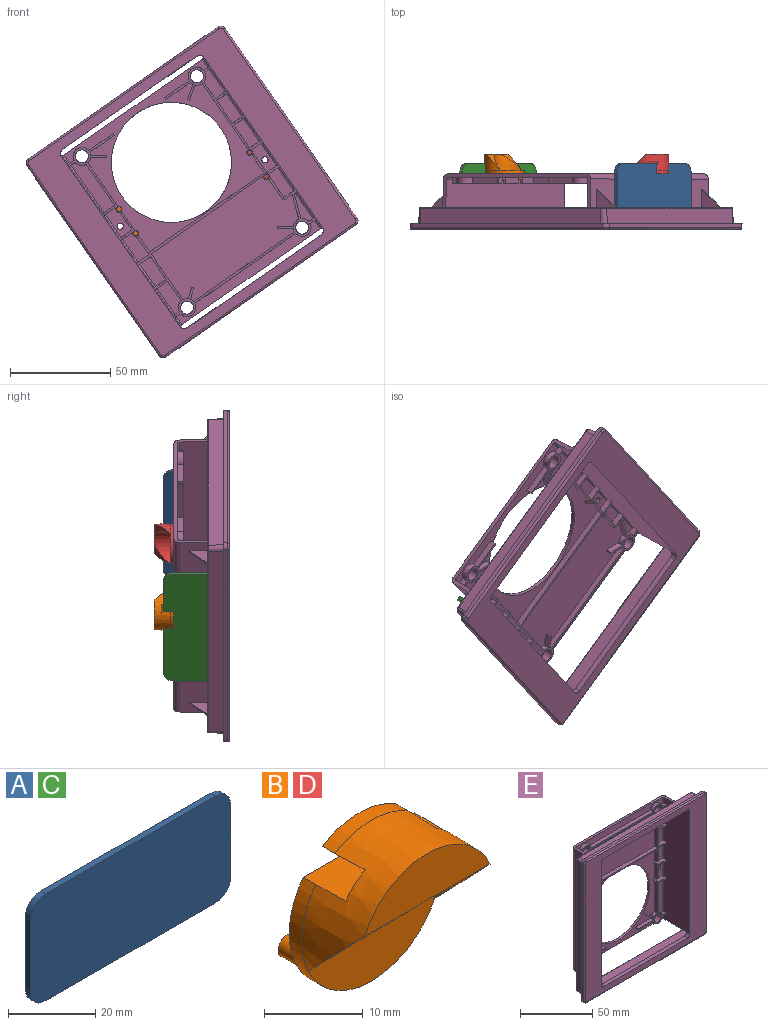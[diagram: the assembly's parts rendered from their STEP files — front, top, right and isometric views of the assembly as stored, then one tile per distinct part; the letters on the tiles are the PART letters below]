
ASSEMBLY  parts=5 mates=6
PART A: 10 faces, bbox 65x1.6x30 mm
  f0: plane 20x1.6mm, normal (1,0,0), area 32mm2, adj f1,f7,f8,f9
  f1: cylinder r=5mm len=5mm, axis (0,1,0), area 12.6mm2, adj f0,f2,f8,f9
  f2: plane 55x1.6mm, normal (0,0,1), area 88mm2, adj f1,f3,f8,f9
  f3: cylinder r=5mm len=5mm, axis (0,1,0), area 12.6mm2, adj f2,f4,f8,f9
  f4: plane 20x1.6mm, normal (-1,0,0), area 32mm2, adj f3,f5,f8,f9
  f5: cylinder r=5mm len=5mm, axis (0,1,0), area 12.6mm2, adj f4,f6,f8,f9
  f6: plane 55x1.6mm, normal (0,0,-1), area 88mm2, adj f5,f7,f8,f9
  f7: cylinder r=5mm len=5mm, axis (0,1,0), area 12.6mm2, adj f0,f6,f8,f9
  f8: plane 65x30mm, normal (0,-1,0), area 1928.5mm2, adj f0,f1,f2,f3,f4,f5,f6,f7
  f9: plane 65x30mm, normal (0,1,0), area 1928.5mm2, adj f0,f1,f2,f3,f4,f5,f6,f7
PART B: 18 faces, bbox 20x12.8x20 mm
  f0: plane 20x16mm, normal (0,1,0), area 252.1mm2, adj f4,f6,f7,f9,f14
  f1: plane 10.54x1.5mm, normal (0,1,0), area 10.7mm2, adj f5,f13
  f2: cone r=10mm half-angle=1deg, axis (0,1,0), area 219.9mm2, adj f4,f5,f12,f13,f14,f15,f16,f17
  f3: plane 18.1x14mm, normal (0,-1,0), area 181.7mm2, adj f4,f6,f11
  f4: cylinder r=10mm len=20mm, axis (0,-1,0), area 79.7mm2, adj f0,f2,f3,f14
  f5: cylinder r=10mm len=10.54mm, axis (0,-1,0), area 20mm2, adj f1,f2,f13
  f6: cylinder r=1.55mm len=3.1mm, axis (0,-1,0), area 17.5mm2, adj f0,f3
  f7: cylinder r=1.25mm len=3mm, axis (0,-1,0), area 23.6mm2, adj f0,f8
  f8: plane 2.5x2.5mm, normal (0,1,0), area 4.9mm2, adj f7
  f9: cylinder r=1.25mm len=3mm, axis (0,-1,0), area 23.6mm2, adj f0,f10
  f10: plane 2.5x2.5mm, normal (0,1,0), area 4.9mm2, adj f9
  f11: cone r=9.09mm half-angle=1deg, axis (0,-1,0), area 139.7mm2, adj f3,f12,f16,f17
  f12: plane 17.99x5.83mm, normal (0,-1,0), area 75.2mm2, adj f2,f11,f16,f17
  f13: plane 10.54x6mm, normal (0,0,-1), area 62.6mm2, adj f1,f2,f5,f15
  f14: plane 16x6mm, normal (0,0,1), area 95.6mm2, adj f0,f2,f4,f15
  f15: plane 15.82x2.5mm, normal (0,1,0), area 33.5mm2, adj f2,f13,f14
  f16: plane 8.54x8.28mm, normal (0,-0.72,-0.69), area 29.8mm2, adj f2,f11,f12
  f17: plane 8.54x8.28mm, normal (0,-0.72,-0.69), area 29.8mm2, adj f2,f11,f12
PART C: same geometry as A
PART D: same geometry as B
PART E: 266 faces, bbox 121.1x27.9x121.1 mm
  f0: plane 85.9x49.43mm, normal (0,-1,0), area 331.9mm2, adj f4,f6,f27,f37,f50,f51,f53,f54
  f1: plane 12x8.52mm, normal (0,-1,0), area 20.6mm2, adj f5,f7,f27,f155,f156,f166,f218,f219
  f2: plane 35.28x27.37mm, normal (0,-1,0), area 91.9mm2, adj f26,f27,f56,f60,f108,f115,f117,f118
  f3: plane 40.31x3mm, normal (1,-0.01,0), area 120.9mm2, adj f25,f49,f113,f216
  f4: plane 10.24x3mm, normal (-1,-0.01,0), area 30.7mm2, adj f0,f49,f162,f219
  f5: plane 11.86x3mm, normal (-1,-0.01,0), area 35.6mm2, adj f1,f49,f218,f219
  f6: plane 11.17x3.01mm, normal (1,-0.01,0), area 33.5mm2, adj f0,f47,f160,f219
  f7: plane 10.89x3.01mm, normal (1,-0.01,0), area 32.6mm2, adj f1,f48,f156,f218
  f8: plane 9.15x2.5mm, normal (0,1,0), area 22.9mm2, adj f18,f190,f212,f213
  f9: plane 90.76x6.11mm, normal (0,1,0), area 553.7mm2, adj f11,f19,f190,f214,f252,f254
  f10: plane 8x2.5mm, normal (0,1,0), area 20mm2, adj f11,f18,f205,f206
  f11: plane 17.24x10.76mm, normal (0,0.01,-1), area 119.9mm2, adj f9,f10,f18,f193,f205,f214,f215,f254
  f12: plane 90.76x6.11mm, normal (0,1,0), area 553.7mm2, adj f15,f21,f187,f203,f258,f264
  f13: plane 10x2.5mm, normal (0,1,0), area 25mm2, adj f22,f187,f201,f202
  f14: plane 70x2.5mm, normal (0,1,0), area 175mm2, adj f22,f197,f198,f199
  f15: plane 17.24x10.76mm, normal (0,0.01,1), area 119.9mm2, adj f12,f22,f23,f185,f194,f203,f204,f264
  f16: plane 7.72x7.51mm, normal (1,0.02,0), area 57.6mm2, adj f17,f91,f247,f256
  f17: plane 111.01x8.88mm, normal (0,1,0), area 303.6mm2, adj f16,f18,f22,f78,f79,f80,f90,f91
  f18: plane 104x22.15mm, normal (-1,0.02,0), area 2260mm2, adj f8,f10,f11,f17,f20,f65,f102,f105
  f19: plane 89.95x7.51mm, normal (1,0.02,0), area 674.8mm2, adj f9,f248,f252,f254
  f20: plane 70x2.5mm, normal (0,1,0), area 175mm2, adj f18,f208,f209,f210
  f21: plane 89.95x7.51mm, normal (-1,0.02,0), area 674.8mm2, adj f12,f249,f258,f264
  f22: plane 104x22.15mm, normal (1,0.02,0), area 2260mm2, adj f13,f14,f15,f17,f23,f65,f100,f105
  f23: plane 7.15x2.5mm, normal (0,1,0), area 17.9mm2, adj f15,f22,f194,f195
  f24: plane 7.72x7.51mm, normal (-1,0.02,0), area 57.6mm2, adj f65,f95,f239,f262
  f25: cone r=4.45mm half-angle=0.5deg, axis (0,1,0), area 11.4mm2, adj f3,f49,f113,f137
  f26: cone r=4.45mm half-angle=0.5deg, axis (0,1,0), area 9.4mm2, adj f2,f49,f135,f165
  f27: plane 104.01x25.12mm, normal (-1,-0.02,0), area 2589.2mm2, adj f0,f1,f2,f28,f29,f30,f31,f59
  f28: cylinder r=0.9mm len=13.9mm, axis (0,0,-1), area 19.4mm2, adj f27,f48,f153,f156
  f29: cylinder r=0.9mm len=13.9mm, axis (0,0,-1), area 19.4mm2, adj f27,f47,f155,f160
  f30: cylinder r=0.9mm len=15.91mm, axis (0,0,-1), area 22.2mm2, adj f27,f45,f129,f157
  f31: cylinder r=0.9mm len=13.9mm, axis (0,0,-1), area 19.4mm2, adj f27,f46,f158,f159
  f32: cylinder r=0.9mm len=13.9mm, axis (0,0,-1), area 19.4mm2, adj f41,f81,f170,f180
  f33: cylinder r=0.9mm len=13.9mm, axis (0,0,-1), area 19.4mm2, adj f42,f81,f171,f172
  f34: cylinder r=0.9mm len=13.9mm, axis (0,0,-1), area 19.4mm2, adj f39,f81,f179,f182
  f35: cylinder r=0.9mm len=13.9mm, axis (0,0,-1), area 19.4mm2, adj f40,f81,f178,f181
  f36: cylinder r=0.9mm len=13.91mm, axis (0,0,-1), area 19.4mm2, adj f38,f81,f133,f183
  f37: cone r=4.45mm half-angle=0.5deg, axis (0,1,0), area 14.2mm2, adj f0,f43,f124,f173
  f38: plane 13.9x5.86mm, normal (0,-1,0), area 72.7mm2, adj f36,f55,f133,f150,f183
  f39: plane 13.9x5.86mm, normal (0,-1,0), area 81.4mm2, adj f34,f145,f179,f182
  f40: plane 13.9x5.86mm, normal (0,-1,0), area 81.4mm2, adj f35,f147,f178,f181
  f41: plane 13.9x5.86mm, normal (0,-1,0), area 73.7mm2, adj f32,f146,f170,f180,f216,f220
  f42: plane 13.9x5.86mm, normal (0,-1,0), area 81.2mm2, adj f33,f148,f171,f172,f217
  f43: plane 74.8x31.75mm, normal (0,-1,0), area 2199.7mm2, adj f37,f50,f51,f112,f123,f124,f125,f141
  f44: plane 15.9x4.98mm, normal (0,-1,0), area 45.3mm2, adj f62,f63,f126,f174,f175
  f45: plane 15.9x6.51mm, normal (0,-1,0), area 92.4mm2, adj f30,f114,f129,f157,f164
  f46: plane 13.9x6.51mm, normal (0,-1,0), area 90.5mm2, adj f31,f158,f159,f167
  f47: plane 13.9x6.51mm, normal (0,-1,0), area 88.9mm2, adj f6,f29,f155,f160,f166,f219
  f48: plane 13.9x6.51mm, normal (0,-1,0), area 81.3mm2, adj f7,f28,f153,f156,f168,f218,f221
  f49: plane 84.02x64.2mm, normal (0,-1,0), area 1560.5mm2, adj f3,f4,f5,f25,f26,f57,f58,f60
  f50: cylinder r=4.45mm len=3mm, axis (0,1,0), area 8.3mm2, adj f0,f43,f142,f163
  f51: cylinder r=4.45mm len=3mm, axis (0,1,0), area 6mm2, adj f0,f43,f141,f143
  f52: plane 84.02x5.05mm, normal (0,-1,0), area 371.7mm2, adj f53,f54,f61,f103,f105,f127,f128,f140
  f53: cone r=4.45mm half-angle=0.5deg, axis (0,1,0), area 38.6mm2, adj f0,f52,f127,f140
  f54: cone r=4.45mm half-angle=0.5deg, axis (0,1,0), area 38.6mm2, adj f0,f52,f128,f140
  f55: cone r=4.45mm half-angle=0.5deg, axis (0,1,0), area 15.8mm2, adj f38,f113,f133,f150
  f56: cone r=4.45mm half-angle=0.5deg, axis (0,1,0), area 17.8mm2, adj f2,f64,f130,f169
  f57: cylinder r=0.9mm len=5.07mm, axis (0,0,-1), area 7.1mm2, adj f49,f81,f106,f132
  f58: cone r=4.45mm half-angle=0.5deg, axis (0,1,0), area 38.8mm2, adj f49,f113,f121,f132
  f59: cylinder r=0.9mm len=28.91mm, axis (0,0,-1), area 40.4mm2, adj f27,f64,f130,f154
  f60: cone r=4.45mm half-angle=0.5deg, axis (0,1,0), area 4.6mm2, adj f2,f49,f118,f134
  f61: cylinder r=0.9mm len=5.07mm, axis (0,0,-1), area 7.1mm2, adj f27,f52,f105,f128
  f62: cylinder r=0.9mm len=15.91mm, axis (0,0,-1), area 22.2mm2, adj f44,f81,f126,f175
  f63: cone r=4.45mm half-angle=0.5deg, axis (0,1,0), area 13mm2, adj f0,f44,f126,f174
  f64: plane 28.9x6.51mm, normal (0,-1,0), area 177mm2, adj f56,f59,f130,f154,f169
  f65: plane 111.01x8.88mm, normal (0,1,0), area 303.6mm2, adj f18,f22,f24,f76,f77,f82,f92,f93
  f66: plane 120.5x120.5mm, normal (0,1,0), area 1523.2mm2, adj f68,f69,f70,f71,f72,f73,f74,f75
  f67: plane 118.5x118.5mm, normal (0,-1,0), area 4621.4mm2, adj f27,f76,f77,f78,f79,f80,f81,f82
  f68: plane 115.5x2mm, normal (0,0,-1), area 231mm2, adj f66,f69,f75,f222
  f69: cylinder r=2.5mm len=2.5mm, axis (0,-1,0), area 7.9mm2, adj f66,f68,f70,f223
  f70: plane 115.5x2mm, normal (1,0,0), area 231mm2, adj f66,f69,f71,f225
  f71: cylinder r=2.5mm len=2.5mm, axis (0,-1,0), area 7.9mm2, adj f66,f70,f72,f227
  f72: plane 115.5x2mm, normal (0,0,1), area 231mm2, adj f66,f71,f73,f229
  f73: cylinder r=2.5mm len=2.5mm, axis (0,-1,0), area 7.9mm2, adj f66,f72,f74,f228
  f74: plane 115.5x2mm, normal (-1,0,0), area 231mm2, adj f66,f73,f75,f226
  f75: cylinder r=2.5mm len=2.5mm, axis (0,-1,0), area 7.9mm2, adj f66,f68,f74,f224
  f76: plane 81.7x3mm, normal (0,-0.02,1), area 245.1mm2, adj f65,f67,f77,f82
  f77: cone r=2.5mm half-angle=1deg, axis (0,-1,0), area 11.7mm2, adj f27,f65,f67,f76
  f78: cone r=2.5mm half-angle=1deg, axis (0,-1,0), area 11.7mm2, adj f17,f27,f67,f79
  f79: plane 81.7x3mm, normal (0,-0.02,-1), area 245.1mm2, adj f17,f67,f78,f80
  f80: cone r=2.5mm half-angle=1deg, axis (0,-1,0), area 11.7mm2, adj f17,f67,f79,f81
  f81: plane 104.01x25.12mm, normal (1,-0.02,0), area 2586.7mm2, adj f0,f32,f33,f34,f35,f36,f57,f62
  f82: cone r=2.5mm half-angle=1deg, axis (0,-1,0), area 11.7mm2, adj f65,f67,f76,f81
  f83: plane 109.5x7.51mm, normal (0,0.02,-1), area 822.3mm2, adj f66,f84,f98,f237
  f84: cone r=2.25mm half-angle=1deg, axis (0,-1,0), area 25.8mm2, adj f66,f83,f85,f235
  f85: plane 109.5x7.51mm, normal (-1,0.02,0), area 822.3mm2, adj f66,f84,f86,f233
  f86: cone r=2.25mm half-angle=1deg, axis (0,-1,0), area 25.8mm2, adj f66,f85,f87,f231
  f87: plane 109.5x7.51mm, normal (0,0.02,1), area 822.3mm2, adj f66,f86,f88,f230
  f88: cone r=2.25mm half-angle=1deg, axis (0,-1,0), area 25.8mm2, adj f66,f87,f89,f232
  f89: plane 109.5x7.51mm, normal (1,0.02,0), area 822.3mm2, adj f66,f88,f98,f234
  f90: plane 109.5x7.51mm, normal (0,0.02,-1), area 822.3mm2, adj f17,f91,f97,f245
  f91: cone r=0.75mm half-angle=1deg, axis (0,1,0), area 9.6mm2, adj f16,f17,f90,f246
  f92: plane 7.72x7.51mm, normal (1,0.02,0), area 57.6mm2, adj f65,f93,f238,f250
  f93: cone r=0.75mm half-angle=1deg, axis (0,1,0), area 9.6mm2, adj f65,f92,f94,f240
  f94: plane 109.5x7.51mm, normal (0,0.02,1), area 822.3mm2, adj f65,f93,f95,f242
  f95: cone r=0.75mm half-angle=1deg, axis (0,1,0), area 9.6mm2, adj f24,f65,f94,f241
  f96: plane 7.72x7.51mm, normal (-1,0.02,0), area 57.6mm2, adj f17,f97,f243,f260
  f97: cone r=0.75mm half-angle=1deg, axis (0,1,0), area 9.6mm2, adj f17,f90,f96,f244
  f98: cone r=2.25mm half-angle=1deg, axis (0,-1,0), area 25.8mm2, adj f66,f83,f89,f236
  f99: plane 112.79x112.79mm, normal (0,1,0), area 109.6mm2, adj f185,f188,f191,f193,f230,f231,f232,f233
  f100: cylinder r=2.7mm len=103.23mm, axis (0,0,-1), area 432.7mm2, adj f22,f101,f105,f106
  f101: plane 103.13x84.02mm, normal (0,1,0), area 5662.2mm2, adj f100,f102,f105,f106,f107,f108,f109,f110
  f102: cylinder r=2.7mm len=103.23mm, axis (0,0,-1), area 432.7mm2, adj f18,f101,f105,f106
  f103: cylinder r=0.9mm len=5.07mm, axis (0,0,-1), area 7.1mm2, adj f52,f81,f105,f127
  f104: cylinder r=0.9mm len=5.07mm, axis (0,0,-1), area 7.1mm2, adj f27,f49,f106,f131
  f105: plane 90.22x24.82mm, normal (0,0.02,1), area 241.1mm2, adj f17,f18,f22,f27,f52,f61,f81,f100
  f106: plane 90.22x24.82mm, normal (0,0.02,-1), area 241mm2, adj f18,f22,f27,f49,f57,f65,f81,f100
  f107: cylinder r=3.25mm len=6.5mm, axis (0,-1,0), area 98mm2, adj f0,f101
  f108: cylinder r=3.25mm len=6.5mm, axis (0,-1,0), area 98mm2, adj f2,f101
  f109: cylinder r=30mm len=60mm, axis (0,-1,0), area 339.3mm2, adj f49,f101
  f110: cylinder r=3.25mm len=6.5mm, axis (0,-1,0), area 98mm2, adj f101,f113
  f111: cylinder r=3.25mm len=6.5mm, axis (0,-1,0), area 98mm2, adj f0,f101
  f112: cone r=4.45mm half-angle=0.5deg, axis (0,1,0), area 4.9mm2, adj f0,f43,f123,f141
  f113: plane 49.97x27.37mm, normal (0,-1,0), area 121.2mm2, adj f3,f25,f55,f58,f81,f110,f116,f120
  f114: cone r=4.45mm half-angle=0.5deg, axis (0,1,0), area 17.8mm2, adj f0,f45,f129,f164
  f115: cone r=4.45mm half-angle=0.5deg, axis (0,1,0), area 38.9mm2, adj f2,f49,f117,f131
  f116: cone r=4.45mm half-angle=0.5deg, axis (0,1,0), area 4.7mm2, adj f49,f113,f120,f138
  f117: plane 15.05x3mm, normal (0,-0.01,-1), area 45.1mm2, adj f2,f49,f115,f119
  f118: plane 15.07x3mm, normal (0,-0.01,1), area 45.1mm2, adj f2,f49,f60,f119
  f119: plane 3x1.1mm, normal (-1,-0.01,0), area 3.2mm2, adj f2,f49,f117,f118
  f120: plane 15.07x3mm, normal (0,-0.01,1), area 45.1mm2, adj f49,f113,f116,f122
  f121: plane 15.05x3mm, normal (0,-0.01,-1), area 45.1mm2, adj f49,f58,f113,f122
  f122: plane 3x1.1mm, normal (1,-0.01,0), area 3.2mm2, adj f49,f113,f120,f121
  f123: plane 6.62x4.61mm, normal (0.57,-0.01,0.82), area 24.1mm2, adj f0,f43,f112,f125
  f124: plane 6.59x4.64mm, normal (-0.57,-0.01,-0.82), area 24.1mm2, adj f0,f37,f43,f125
  f125: plane 3x0.9mm, normal (0.82,-0.01,-0.57), area 3.2mm2, adj f0,f43,f123,f124
  f126: plane 3.56x3mm, normal (0,-0.01,-1), area 10.4mm2, adj f0,f44,f62,f63,f81
  f127: plane 3.56x3mm, normal (0,-0.01,1), area 10.4mm2, adj f0,f52,f53,f81,f103
  f128: plane 3.56x3mm, normal (0,-0.01,1), area 10.4mm2, adj f0,f27,f52,f54,f61
  f129: plane 3.56x3mm, normal (0,-0.01,-1), area 10.4mm2, adj f0,f27,f30,f45,f114
  f130: plane 3.56x3mm, normal (0,-0.01,1), area 10.4mm2, adj f2,f27,f56,f59,f64
  f131: plane 3.56x3mm, normal (0,-0.01,-1), area 10.4mm2, adj f2,f27,f49,f104,f115
  f132: plane 3.56x3mm, normal (0,-0.01,-1), area 10.4mm2, adj f49,f57,f58,f81,f113
  f133: plane 3.56x3mm, normal (0,-0.01,1), area 10.4mm2, adj f36,f38,f55,f81,f113
  f134: plane 6.62x4.61mm, normal (-0.57,-0.01,-0.82), area 24.1mm2, adj f2,f49,f60,f136
  f135: plane 6.59x4.64mm, normal (0.57,-0.01,0.82), area 24.1mm2, adj f2,f26,f49,f136
  f136: plane 3x0.9mm, normal (-0.82,-0.01,0.57), area 3.2mm2, adj f2,f49,f134,f135
  f137: plane 6.59x4.64mm, normal (-0.57,-0.01,0.82), area 24.1mm2, adj f25,f49,f113,f139
  f138: plane 6.62x4.61mm, normal (0.57,-0.01,-0.82), area 24.1mm2, adj f49,f113,f116,f139
  f139: plane 3x0.9mm, normal (0.82,-0.01,0.57), area 3.2mm2, adj f49,f113,f137,f138
  f140: plane 61.21x3mm, normal (0,-0.01,1), area 183.6mm2, adj f0,f52,f53,f54
  f141: plane 61.19x3mm, normal (0,-0.01,-1), area 183.5mm2, adj f0,f43,f51,f112
  f142: plane 4.64x3.88mm, normal (0.64,-0.01,-0.77), area 18.1mm2, adj f0,f43,f50,f144
  f143: plane 4.65x3.86mm, normal (-0.64,-0.01,0.77), area 18.1mm2, adj f0,f43,f51,f144
  f144: plane 3x0.85mm, normal (-0.77,-0.01,-0.64), area 3.2mm2, adj f0,f43,f142,f143
  f145: plane 13.9x3mm, normal (-1,-0.01,0), area 41.7mm2, adj f39,f113,f179,f182
  f146: plane 12.55x3.04mm, normal (-1,-0.01,0), area 37.4mm2, adj f0,f41,f170,f216
  f147: plane 13.9x3mm, normal (-1,-0.01,0), area 41.7mm2, adj f40,f113,f178,f181
  f148: plane 12.82x3.04mm, normal (-1,-0.01,0), area 38.3mm2, adj f0,f42,f172,f217
  f149: plane 10.91x3mm, normal (1,-0.01,0), area 32.7mm2, adj f0,f49,f162,f216
  f150: plane 10.17x3mm, normal (-1,-0.01,0), area 30.5mm2, adj f38,f55,f113,f183
  f151: plane 12.58x3mm, normal (1,-0.01,0), area 37.7mm2, adj f0,f43,f152,f217
  f152: plane 3x0.55mm, normal (0,0,1), area 1.6mm2, adj f0,f43,f151,f177
  f153: plane 7.47x3mm, normal (0,0,1), area 22.1mm2, adj f2,f27,f28,f48,f168
  f154: plane 7.47x3mm, normal (0,0,-1), area 22.1mm2, adj f2,f27,f59,f64,f169
  f155: plane 7.47x3mm, normal (0,0,1), area 22.1mm2, adj f1,f27,f29,f47,f166
  f156: plane 7.47x3mm, normal (0,0,-1), area 22.1mm2, adj f1,f7,f27,f28,f48
  f157: plane 7.47x3mm, normal (0,0,1), area 22.1mm2, adj f0,f27,f30,f45,f164
  f158: plane 7.47x3mm, normal (0,0,-1), area 22.1mm2, adj f0,f27,f31,f46,f167
  f159: plane 7.47x3mm, normal (0,0,1), area 22.1mm2, adj f0,f27,f31,f46,f167
  f160: plane 7.47x3mm, normal (0,0,-1), area 22.1mm2, adj f0,f6,f27,f29,f47
  f161: plane 68.42x3mm, normal (0,0,1), area 205.2mm2, adj f0,f43,f163,f217
  f162: plane 69.51x3mm, normal (0,0,-1), area 208.4mm2, adj f0,f4,f49,f149
  f163: plane 27.89x3mm, normal (-1,-0.01,0), area 83.7mm2, adj f0,f43,f50,f161
  f164: plane 12.05x3mm, normal (1,-0.01,0), area 36.1mm2, adj f0,f45,f114,f157
  f165: plane 26.4x3mm, normal (-1,-0.01,0), area 79.1mm2, adj f2,f26,f49,f218
  f166: plane 3.01x0.04mm, normal (1,-0.01,0), area 0.1mm2, adj f1,f47,f155,f219
  f167: plane 13.9x3mm, normal (1,-0.01,0), area 41.7mm2, adj f0,f46,f158,f159
  f168: plane 3.01x0.32mm, normal (1,-0.01,0), area 0.9mm2, adj f2,f48,f153,f218
  f169: plane 25.05x3mm, normal (1,-0.01,0), area 75.1mm2, adj f2,f56,f64,f154
  f170: plane 6.82x3mm, normal (0,0,-1), area 20.2mm2, adj f0,f32,f41,f81,f146
  f171: plane 6.65x3mm, normal (0,0,1), area 19.7mm2, adj f0,f33,f42,f81,f217
  f172: plane 6.82x3mm, normal (0,0,-1), area 20.2mm2, adj f0,f33,f42,f81,f148
  f173: plane 12.14x4.44mm, normal (0.94,-0.01,-0.34), area 38.7mm2, adj f0,f37,f43,f176
  f174: plane 12.5x4.58mm, normal (-0.94,-0.01,0.34), area 39.9mm2, adj f0,f44,f63,f175
  f175: plane 3x1.4mm, normal (0,0,1), area 3.9mm2, adj f0,f44,f62,f81,f174
  f176: plane 4.82x3mm, normal (0,0,1), area 14.4mm2, adj f0,f43,f173,f177
  f177: plane 3x0.55mm, normal (1,0,0), area 1.6mm2, adj f0,f43,f152,f176
  f178: plane 6.82x3mm, normal (0,0,1), area 20.2mm2, adj f35,f40,f81,f113,f147
  f179: plane 6.82x3mm, normal (0,0,-1), area 20.2mm2, adj f34,f39,f81,f113,f145
  f180: plane 6.76x3mm, normal (0,0,1), area 20mm2, adj f32,f41,f81,f113,f216
  f181: plane 6.82x3mm, normal (0,0,-1), area 20.2mm2, adj f35,f40,f81,f113,f147
  f182: plane 6.82x3mm, normal (0,0,1), area 20.2mm2, adj f34,f39,f81,f113,f145
  f183: plane 6.82x3mm, normal (0,0,-1), area 20.2mm2, adj f36,f38,f81,f113,f150
  f184: plane 17.24x10.76mm, normal (0,0.01,-1), area 128.9mm2, adj f22,f65,f185,f262,f263
  f185: plane 10.85x9.11mm, normal (0.64,0.77,0), area 13.1mm2, adj f15,f22,f99,f184,f263,f265
  f186: plane 17.24x10.76mm, normal (0,0.01,1), area 128.9mm2, adj f17,f22,f188,f260,f261
  f187: plane 17.24x10.76mm, normal (0,0.01,-1), area 119.9mm2, adj f12,f13,f22,f188,f202,f203,f204,f258
  f188: plane 10.85x9.11mm, normal (0.64,0.77,0), area 13.1mm2, adj f22,f99,f186,f187,f259,f261
  f189: plane 17.24x10.76mm, normal (0,0.01,-1), area 128.9mm2, adj f18,f65,f191,f250,f251
  f190: plane 17.24x10.76mm, normal (0,0.01,1), area 119.9mm2, adj f8,f9,f18,f191,f213,f214,f215,f252
  f191: plane 10.85x9.11mm, normal (-0.64,0.77,0), area 13.1mm2, adj f18,f99,f189,f190,f251,f253
  f192: plane 17.24x10.76mm, normal (0,0.01,1), area 128.9mm2, adj f17,f18,f193,f256,f257
  f193: plane 10.85x9.11mm, normal (-0.64,0.77,0), area 13.1mm2, adj f11,f18,f99,f192,f255,f257
  f194: plane 7.22x5mm, normal (-1,0,0), area 35.9mm2, adj f15,f23,f195,f204
  f195: plane 5x2.5mm, normal (0,0,-1), area 12.5mm2, adj f23,f194,f196,f204
  f196: plane 5x1.8mm, normal (-1,0,0), area 9mm2, adj f22,f195,f197,f204
  f197: plane 5x2.5mm, normal (0,0,1), area 12.5mm2, adj f14,f196,f198,f204
  f198: plane 70x5mm, normal (-1,0,0), area 350mm2, adj f14,f197,f199,f204
  f199: plane 5x2.5mm, normal (0,0,-1), area 12.5mm2, adj f14,f198,f200,f204
  f200: plane 5x1.8mm, normal (-1,0,0), area 9mm2, adj f22,f199,f201,f204
  f201: plane 5x2.5mm, normal (0,0,1), area 12.5mm2, adj f13,f200,f202,f204
  f202: plane 10.07x5mm, normal (-1,0,0), area 50.2mm2, adj f13,f187,f201,f204
  f203: plane 90.88x5mm, normal (1,0,0), area 454.1mm2, adj f12,f15,f187,f204
  f204: plane 90.88x4.3mm, normal (0,1,0), area 172.6mm2, adj f15,f187,f194,f195,f196,f197,f198,f199
  f205: plane 8.07x5mm, normal (1,0,0), area 40.2mm2, adj f10,f11,f206,f215
  f206: plane 5x2.5mm, normal (0,0,1), area 12.5mm2, adj f10,f205,f207,f215
  f207: plane 5x1.8mm, normal (1,0,0), area 9mm2, adj f18,f206,f208,f215
  f208: plane 5x2.5mm, normal (0,0,-1), area 12.5mm2, adj f20,f207,f209,f215
  f209: plane 70x5mm, normal (1,0,0), area 350mm2, adj f20,f208,f210,f215
  f210: plane 5x2.5mm, normal (0,0,1), area 12.5mm2, adj f20,f209,f211,f215
  f211: plane 5x1.8mm, normal (1,0,0), area 9mm2, adj f18,f210,f212,f215
  f212: plane 5x2.5mm, normal (0,0,-1), area 12.5mm2, adj f8,f211,f213,f215
  f213: plane 9.22x5mm, normal (1,0,0), area 45.9mm2, adj f8,f190,f212,f215
  f214: plane 90.88x5mm, normal (-1,0,0), area 454.1mm2, adj f9,f11,f190,f215
  f215: plane 90.88x4.3mm, normal (0,1,0), area 172.6mm2, adj f11,f190,f205,f206,f207,f208,f209,f210
  f216: cylinder r=1.5mm len=4.8mm, axis (0,1,0), area 25.3mm2, adj f0,f3,f41,f49,f101,f113,f146,f149
  f217: cylinder r=1.5mm len=4.8mm, axis (0,1,0), area 29.6mm2, adj f0,f42,f43,f101,f148,f151,f161,f171
  f218: cylinder r=1.5mm len=4.8mm, axis (0,1,0), area 23.6mm2, adj f1,f2,f5,f7,f48,f49,f101,f165
  f219: cylinder r=1.5mm len=4.8mm, axis (0,1,0), area 23.6mm2, adj f0,f1,f4,f5,f6,f47,f49,f101
  f220: cylinder r=1.55mm len=3.1mm, axis (0,1,0), area 17.5mm2, adj f41,f101
  f221: cylinder r=1.55mm len=3.1mm, axis (0,1,0), area 17.5mm2, adj f48,f101
  f222: cylinder r=1mm len=115.5mm, axis (1,0,0), area 181.4mm2, adj f67,f68,f223,f224
  f223: torus R=1.5mm, axis (0,-1,0), area 5.3mm2, adj f67,f69,f222,f225
  f224: torus R=1.5mm, axis (0,-1,0), area 5.3mm2, adj f67,f75,f222,f226
  f225: cylinder r=1mm len=115.5mm, axis (0,0,1), area 181.4mm2, adj f67,f70,f223,f227
  f226: cylinder r=1mm len=115.5mm, axis (0,0,-1), area 181.4mm2, adj f67,f74,f224,f228
  f227: torus R=1.5mm, axis (0,-1,0), area 5.3mm2, adj f67,f71,f225,f229
  f228: torus R=1.5mm, axis (0,-1,0), area 5.3mm2, adj f67,f73,f226,f229
  f229: cylinder r=1mm len=115.5mm, axis (-1,0,0), area 181.4mm2, adj f67,f72,f227,f228
  f230: cylinder r=0.5mm len=109.5mm, axis (1,0,0), area 85mm2, adj f87,f99,f231,f232
  f231: torus R=1.62mm, axis (0,1,0), area 2.4mm2, adj f86,f99,f230,f233
  f232: torus R=1.62mm, axis (0,1,0), area 2.4mm2, adj f88,f99,f230,f234
  f233: cylinder r=0.5mm len=109.5mm, axis (0,0,-1), area 85mm2, adj f85,f99,f231,f235
  f234: cylinder r=0.5mm len=109.5mm, axis (0,0,-1), area 85mm2, adj f89,f99,f232,f236
  f235: torus R=1.62mm, axis (0,1,0), area 2.4mm2, adj f84,f99,f233,f237
  f236: torus R=1.62mm, axis (0,1,0), area 2.4mm2, adj f98,f99,f234,f237
  f237: cylinder r=0.5mm len=109.5mm, axis (1,0,0), area 85mm2, adj f83,f99,f235,f236
  f238: cylinder r=0.5mm len=7.74mm, axis (0,0,-1), area 6mm2, adj f92,f99,f240,f251
  f239: cylinder r=0.5mm len=7.74mm, axis (0,0,-1), area 6mm2, adj f24,f99,f241,f263
  f240: torus R=1.38mm, axis (0,1,0), area 1.3mm2, adj f93,f99,f238,f242
  f241: torus R=1.38mm, axis (0,1,0), area 1.3mm2, adj f95,f99,f239,f242
  f242: cylinder r=0.5mm len=109.5mm, axis (1,0,0), area 85mm2, adj f94,f99,f240,f241
  f243: cylinder r=0.5mm len=7.74mm, axis (0,0,-1), area 6mm2, adj f96,f99,f244,f261
  f244: torus R=1.38mm, axis (0,1,0), area 1.3mm2, adj f97,f99,f243,f245
  f245: cylinder r=0.5mm len=109.5mm, axis (1,0,0), area 85mm2, adj f90,f99,f244,f246
  f246: torus R=1.38mm, axis (0,1,0), area 1.3mm2, adj f91,f99,f245,f247
  f247: cylinder r=0.5mm len=7.74mm, axis (0,0,-1), area 6mm2, adj f16,f99,f246,f257
  f248: cylinder r=0.5mm len=89.97mm, axis (0,0,-1), area 69.9mm2, adj f19,f99,f253,f255
  f249: cylinder r=0.5mm len=89.97mm, axis (0,0,-1), area 69.9mm2, adj f21,f99,f259,f265
  f250: cylinder r=0.5mm len=7.52mm, axis (-0.02,1,0.01), area 5.9mm2, adj f65,f92,f189,f251
  f251: bspline ~1.17x1.04mm, area 0.5mm2, adj f99,f189,f191,f238,f250
  f252: cylinder r=0.5mm len=7.52mm, axis (-0.02,1,-0.01), area 5.9mm2, adj f9,f19,f190,f253
  f253: bspline ~1.04x1mm, area 0.5mm2, adj f99,f190,f191,f248,f252
  f254: cylinder r=0.5mm len=7.52mm, axis (-0.02,1,0.01), area 5.9mm2, adj f9,f11,f19,f255
  f255: bspline ~1.17x1.04mm, area 0.5mm2, adj f11,f99,f193,f248,f254
  f256: cylinder r=0.5mm len=7.52mm, axis (-0.02,1,-0.01), area 5.9mm2, adj f16,f17,f192,f257
  f257: bspline ~1.04x1mm, area 0.5mm2, adj f99,f192,f193,f247,f256
  f258: cylinder r=0.5mm len=7.52mm, axis (-0.02,-1,-0.01), area 5.9mm2, adj f12,f21,f187,f259
  f259: bspline ~1.04x1.04mm, area 0.5mm2, adj f99,f187,f188,f249,f258
  f260: cylinder r=0.5mm len=7.52mm, axis (-0.02,-1,0.01), area 5.9mm2, adj f17,f96,f186,f261
  f261: bspline ~1.04x1mm, area 0.5mm2, adj f99,f186,f188,f243,f260
  f262: cylinder r=0.5mm len=7.52mm, axis (-0.02,-1,-0.01), area 5.9mm2, adj f24,f65,f184,f263
  f263: bspline ~1.04x1.04mm, area 0.5mm2, adj f99,f184,f185,f239,f262
  f264: cylinder r=0.5mm len=7.52mm, axis (-0.02,-1,0.01), area 5.9mm2, adj f12,f15,f21,f265
  f265: bspline ~1.04x1mm, area 0.5mm2, adj f15,f99,f185,f249,f264
PLACE A rot(axis=(0.35,-0.66,0.66),141.8deg) t=(217.05,272.26,135.91)mm
PLACE B rot(axis=(-0.89,0,0.46),180deg) t=(133.49,310.6,106.06)mm
PLACE C rot(axis=(-0.8,0.42,0.42),102.4deg) t=(121.3,273.73,111.24)mm
PLACE D rot(axis=(0.46,0,0.89),180deg) t=(207.32,310.6,140.36)mm
PLACE E rot(axis=(0,1,0),145.2deg) t=(170.08,255,123.68)mm
MATE slider A.f2 <-> E.f20  axis (0,-1,0) through (208.45,258,149.67)mm
MATE slider D.f2 <-> E.f220  axis (0,-1,0) through (206.5,282.8,139.79)mm
MATE slider C.f6 <-> E.f14  axis (0,-1,0) through (131.21,258,98.39)mm
MATE slider E.f218 <-> B.f9  axis (0,1,0) through (133.6,282.8,115.1)mm
MATE slider B.f2 <-> E.f221  axis (0,-1,0) through (134.31,282.8,106.63)mm
MATE slider D.f7 <-> E.f216  axis (0,-1,0) through (198.81,279.8,143.4)mm
